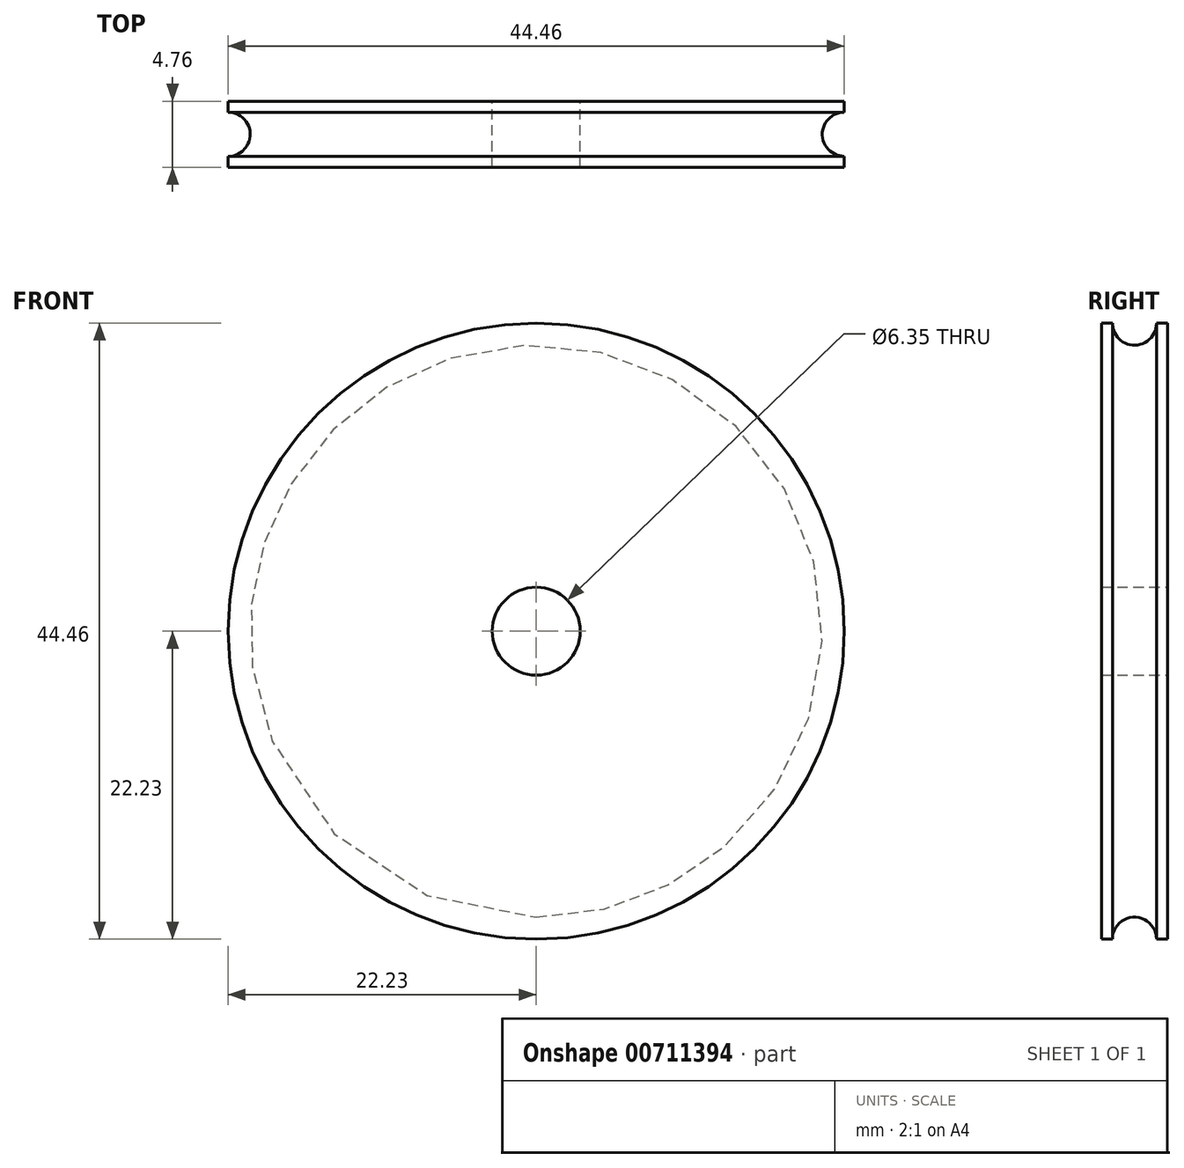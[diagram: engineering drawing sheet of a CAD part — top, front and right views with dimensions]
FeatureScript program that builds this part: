
annotation { "Feature Type Name" : "Feature", "Feature Type Description" : "" }
export const myFeature = defineFeature(function(context is Context, id is Id, definition is map)
    precondition{}
    {
        {
            var Q0;
            Q0=qCreatedBy(makeId("Front.planeOp"),FACE);
            var sketch = newSketch(context, id + "F0", { "sketchPlane" : qUnion([Q0])});
            skCircle(sketch, "E0", {"center": v(0, 0) * mm, "radius": 22.23 * mm});
            skCircle(sketch, "E1", {"center": v(0, 0) * mm, "radius": 3.18 * mm});
            skSolve(sketch);
        }
        {
            var Q0;
            Q0=makeQuery(id+"F0.imprint","IMPRINT",FACE,{"disambiguationData":[TD([[makeQuery(id+"F0.imprint","IMPRINT",EDGE,{"derivedFrom":sQuery(id+"F0.wireOp",EDGE,"E0")}),1.0]])]});
            extrude(context, id + "F1", {"entities" : qUnion([Q0]), "depth" : 4.76 * mm, "offsetDistance" : 25.4 * mm});
        }
        {
            var Q0;
            Q0=qCreatedBy(makeId("Right.planeOp"),FACE);
            var sketch = newSketch(context, id + "F2", { "sketchPlane" : qUnion([Q0])});
            skCircle(sketch, "E2", {"center": v(-2.38, 22.23) * mm, "radius": 1.59 * mm});
            skSolve(sketch);
        }
        {
            var Q0;
            Q0 = qSketchRegion(id + "F2", true);
            var Q1;
            Q1=makeQuery(id+"F1.opExtrude","CAP_EDGE",EDGE,{"disambiguationData":[OSD([sQuery(id+"F0.wireOp",EDGE,"E1")])],"isStart":false});
            revolve(context, id + "F3", {"operationType" : NewBodyOperationType.REMOVE, "surfaceOperationType" : NewSurfaceOperationType.NEW, "entities" : qUnion([Q0]), "axis" : qUnion([Q1]), "revolveType" : RevolveType.FULL, "oppositeDirection" : true});
        }
    });
